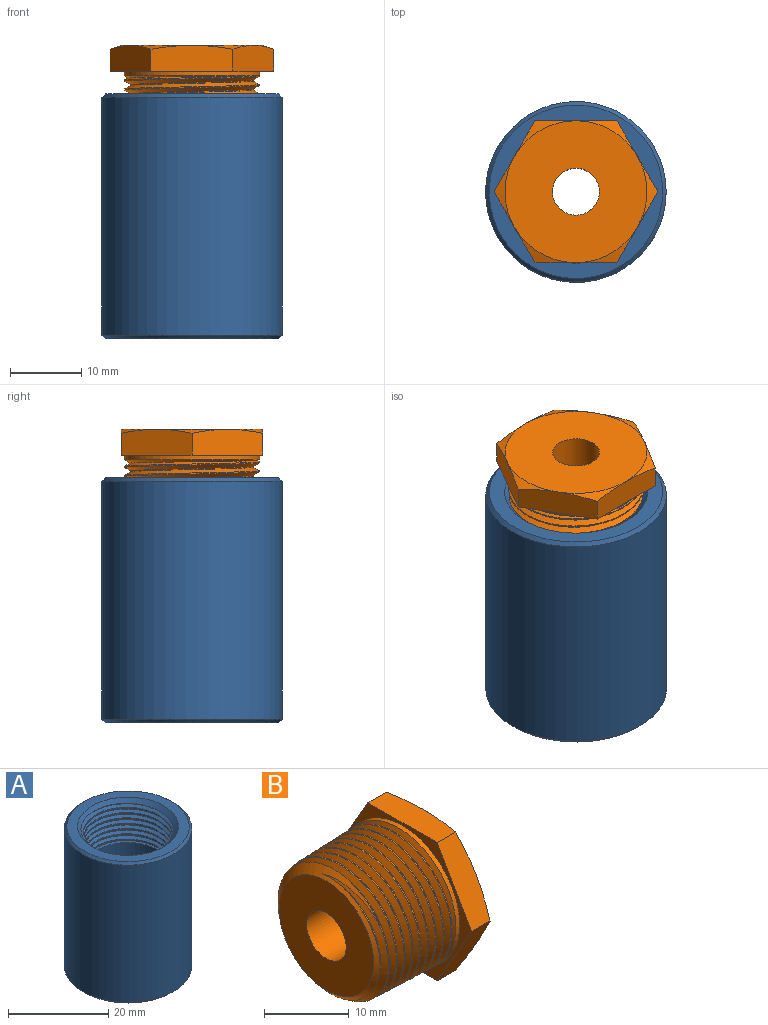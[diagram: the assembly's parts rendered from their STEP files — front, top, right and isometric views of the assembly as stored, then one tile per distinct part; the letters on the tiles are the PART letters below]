
ASSEMBLY  parts=2 mates=1
PART A: 18 faces, bbox 25.7x25.7x34.8 mm
  f0: cylinder r=8.41mm len=16.83mm, axis (0,0,1), area 774.6mm2, adj f13,f17
  f1: cone r=12.2mm half-angle=45deg, axis (0,0,-1), area 55.8mm2, adj f7,f9
  f2: cone r=12.7mm half-angle=45deg, axis (0,0,1), area 55.8mm2, adj f7,f8
  f3: cone r=9.54mm half-angle=1.8deg, axis (0,0,-1), area 77.5mm2, adj f4,f15,f16,f17
  f4: cone r=10.05mm half-angle=45deg, axis (0,0,-1), area 76.2mm2, adj f3,f8,f14,f15,f16
  f5: cone r=9.54mm half-angle=1.8deg, axis (0,0,1), area 77.5mm2, adj f6,f10,f12,f13
  f6: cone r=10.05mm half-angle=45deg, axis (0,0,1), area 76.2mm2, adj f5,f9,f10,f11,f12
  f7: cylinder r=12.7mm len=33.46mm, axis (0,0,-1), area 2670.1mm2, adj f1,f2
  f8: plane 24.39x24.39mm, normal (0,0,-1), area 150mm2, adj f2,f4
  f9: plane 24.39x24.39mm, normal (0,0,1), area 150mm2, adj f1,f6
  f10: bspline ~19.21x19.19mm, area 170.9mm2, adj f5,f6,f11,f13
  f11: bspline ~17.85x17.85mm, area 128.8mm2, adj f6,f10,f12,f13
  f12: bspline ~19.2x19.14mm, area 312.2mm2, adj f5,f6,f11,f13
  f13: plane 18.15x18.05mm, normal (0,0,1), area 24.9mm2, adj f0,f5,f10,f11,f12
  f14: bspline ~17.85x17.85mm, area 128.8mm2, adj f4,f15,f16,f17
  f15: bspline ~19.21x19.19mm, area 170.9mm2, adj f3,f4,f14,f17
  f16: bspline ~19.2x19.14mm, area 312.2mm2, adj f3,f4,f14,f17
  f17: plane 18.15x18.05mm, normal (0,0,-1), area 24.9mm2, adj f0,f3,f14,f15,f16
PART B: 23 faces, bbox 17.9x23.9x23.9 mm
  f0: cylinder r=9.54mm len=19.09mm, axis (-1,0,0), area 37.8mm2, adj f1,f15
  f1: cone r=9.54mm half-angle=60deg, axis (1,0,0), area 29.3mm2, adj f0,f3,f11,f12,f13
  f2: cone r=7.89mm half-angle=50deg, axis (1,0,0), area 59.7mm2, adj f3,f11,f12,f13,f14
  f3: cone r=9.15mm half-angle=1.8deg, axis (1,0,0), area 83.4mm2, adj f1,f2,f11,f12
  f4: plane 19.96x19.96mm, normal (1,0,0), area 278.6mm2, adj f16,f17,f18,f19,f20,f21,f22
  f5: plane 12.4x4.51mm, normal (0,0,-1), area 39.6mm2, adj f6,f10,f15,f16,f21
  f6: plane 10.86x6.64mm, normal (0,0.87,-0.5), area 39.6mm2, adj f5,f7,f15,f20,f21
  f7: plane 10.86x6.65mm, normal (0,0.87,0.5), area 39.6mm2, adj f6,f8,f15,f19,f20
  f8: plane 12.4x4.51mm, normal (0,0,1), area 39.6mm2, adj f7,f9,f15,f18,f19
  f9: plane 10.86x6.64mm, normal (0,-0.87,0.5), area 39.6mm2, adj f8,f10,f15,f17,f18
  f10: plane 10.86x6.65mm, normal (0,-0.87,-0.5), area 39.6mm2, adj f5,f9,f15,f16,f17
  f11: bspline ~19.42x19.3mm, area 477.8mm2, adj f1,f2,f3,f13
  f12: bspline ~20.82x20.67mm, area 840.6mm2, adj f1,f2,f3,f13
  f13: bspline ~17.24x17.17mm, area 74.9mm2, adj f1,f2,f11,f12
  f14: plane 15.79x15.79mm, normal (-1,0,0), area 161.4mm2, adj f2,f22
  f15: plane 23.04x19.96mm, normal (-1,0,0), area 58.8mm2, adj f0,f5,f6,f7,f8,f9,f10
  f16: cone r=9.98mm half-angle=70deg, axis (-1,0,0), area 9mm2, adj f4,f5,f10
  f17: cone r=9.98mm half-angle=70deg, axis (-1,0,0), area 9mm2, adj f4,f9,f10
  f18: cone r=9.98mm half-angle=70deg, axis (-1,0,0), area 9mm2, adj f4,f8,f9
  f19: cone r=9.98mm half-angle=70deg, axis (-1,0,0), area 9mm2, adj f4,f7,f8
  f20: cone r=9.98mm half-angle=70deg, axis (-1,0,0), area 9mm2, adj f4,f6,f7
  f21: cone r=9.98mm half-angle=70deg, axis (-1,0,0), area 9mm2, adj f4,f5,f6
  f22: cylinder r=3.3mm len=16.33mm, axis (1,0,0), area 338.8mm2, adj f4,f14
PLACE A t=(-11.03,-1.82,3.41)mm
PLACE B rot(axis=(-0.58,-0.58,-0.58),120deg) t=(-11.03,-1.82,19.29)mm
MATE fastened B.f3 <-> A.f0  axis (0,0,-1) through (-11.03,-1.82,23.83)mm
